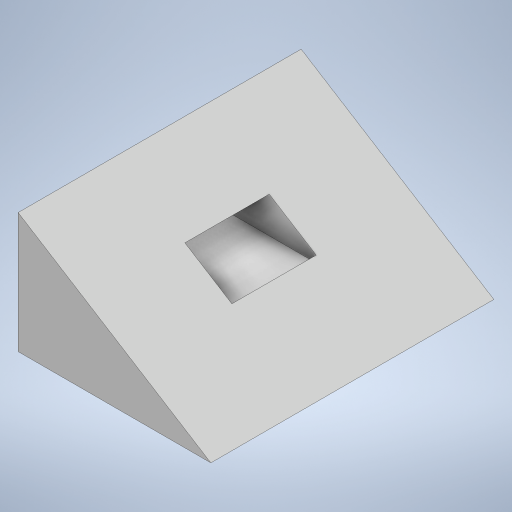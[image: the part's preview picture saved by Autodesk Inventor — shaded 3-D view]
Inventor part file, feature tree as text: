
AUTODESK INVENTOR PART (.ipt)
format: ipt  version: 2024.2 (Build 282272000, 272)  size: 196,096 bytes
history: native  units: in
note: dims shown in document units (in); Inventor stores cm internally (conversion verified against a paired STEP export)
features: extrude x2, sketch x2
ambient origin geometry x8: Origin, YZ Plane, XZ Plane, XY Plane, X Axis, Y Axis, Z Axis, Center Point
bodies: Solid1 (feature_tree)
feature tree (4):
  extrude  "Extrusion1"  Depth=1.2598in
  extrude  "Extrusion2"  Depth=0.748in
  sketch  "Sketch1"  dims[d0=0.7874in d1=1.2598in]
  sketch  "Sketch2"  dims[d2=1.8504in d3=0.0in d5=0.2756in d6=0.6in d7=0.748in d8=0.0in]
